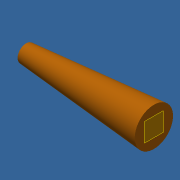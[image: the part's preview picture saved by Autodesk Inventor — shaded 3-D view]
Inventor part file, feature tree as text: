
AUTODESK INVENTOR PART (.ipt)
format: ipt  version: 2018 (Build 220112000, 112)  size: 87,552 bytes
history: native  units: mm
features: sketch x2, plane x1, loft x1
ambient origin geometry x8: Origin, YZ Plane, XZ Plane, XY Plane, X Axis, Y Axis, Z Axis, Center Point
bodies: Solid1 (feature_tree)
feature tree (4):
  sketch  "Sketch1"  dims[d0=20.0mm d1=150.0mm]
  plane  "Work Plane1"
  loft  "Loft1"
  sketch  "Sketch2"  dims[d2=45.0mm d3=0.0mm d4=90.0deg d5=0.0mm d6=90.0deg]
